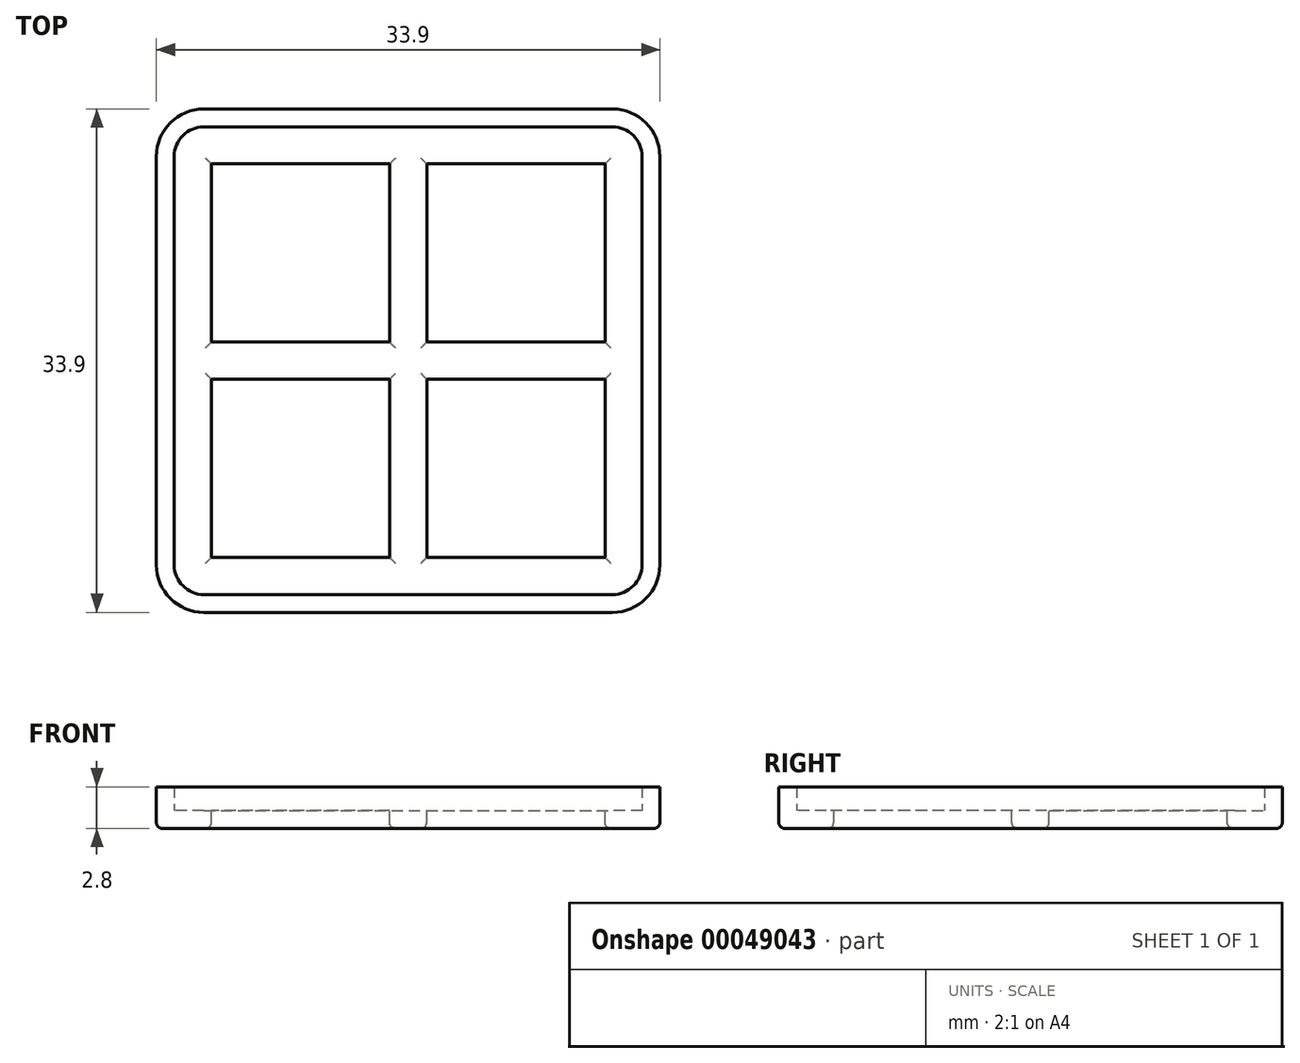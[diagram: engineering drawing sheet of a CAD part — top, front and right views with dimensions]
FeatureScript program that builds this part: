
annotation { "Feature Type Name" : "Feature", "Feature Type Description" : "" }
export const myFeature = defineFeature(function(context is Context, id is Id, definition is map)
    precondition{}
    {
        {
            var Q0;
            Q0=qCreatedBy(makeId("Top.planeOp"),FACE);
            var sketch = newSketch(context, id + "F0", { "sketchPlane" : qUnion([Q0])});
            skLineSegment(sketch, "E0.bottom", {"start": v(0, 0) * mm, "end": v(12, 0) * mm});
            skLineSegment(sketch, "E0.top", {"start": v(0, 12) * mm, "end": v(12, 12) * mm});
            skLineSegment(sketch, "E0.left", {"start": v(0, 0) * mm, "end": v(0, 12) * mm});
            skLineSegment(sketch, "E0.right", {"start": v(12, 0) * mm, "end": v(12, 12) * mm});
            skLineSegment(sketch, "E1.bottom", {"start": v(12, -2.5) * mm, "end": v(0, -2.5) * mm});
            skLineSegment(sketch, "E1.top", {"start": v(12, -14.5) * mm, "end": v(0, -14.5) * mm});
            skLineSegment(sketch, "E1.left", {"start": v(12, -2.5) * mm, "end": v(12, -14.5) * mm});
            skLineSegment(sketch, "E1.right", {"start": v(0, -2.5) * mm, "end": v(0, -14.5) * mm});
            skLineSegment(sketch, "E2.bottom", {"start": v(-2.5, 12) * mm, "end": v(-14.5, 12) * mm});
            skLineSegment(sketch, "E2.top", {"start": v(-2.5, 0) * mm, "end": v(-14.5, 0) * mm});
            skLineSegment(sketch, "E2.left", {"start": v(-2.5, 12) * mm, "end": v(-2.5, 0) * mm});
            skLineSegment(sketch, "E2.right", {"start": v(-14.5, 12) * mm, "end": v(-14.5, 0) * mm});
            skLineSegment(sketch, "E3.bottom", {"start": v(-2.5, -2.5) * mm, "end": v(-14.5, -2.5) * mm});
            skLineSegment(sketch, "E3.top", {"start": v(-2.5, -14.5) * mm, "end": v(-14.5, -14.5) * mm});
            skLineSegment(sketch, "E3.left", {"start": v(-2.5, -2.5) * mm, "end": v(-2.5, -14.5) * mm});
            skLineSegment(sketch, "E3.right", {"start": v(-14.5, -2.5) * mm, "end": v(-14.5, -14.5) * mm});
            skLineSegment(sketch, "E4.bottom", {"start": v(-15, 14.5) * mm, "end": v(12.5, 14.5) * mm});
            skLineSegment(sketch, "E4.top", {"start": v(-15, -17) * mm, "end": v(12.5, -17) * mm});
            skLineSegment(sketch, "E4.left", {"start": v(-17, 12.5) * mm, "end": v(-17, -15) * mm});
            skLineSegment(sketch, "E4.right", {"start": v(14.5, 12.5) * mm, "end": v(14.5, -15) * mm});
            skPoint(sketch, "E5.visualSharp", {"position": v(-17, 14.5) * mm});
            skArc(sketch, "E5.filletArc", {"start": v(-15, 14.5) * mm, "mid": v(-16.41, 13.91) * mm, "end": v(-17, 12.5) * mm});
            skPoint(sketch, "E6.visualSharp", {"position": v(14.5, 14.5) * mm});
            skArc(sketch, "E6.filletArc", {"start": v(14.5, 12.5) * mm, "mid": v(13.91, 13.91) * mm, "end": v(12.5, 14.5) * mm});
            skPoint(sketch, "E7.visualSharp", {"position": v(14.5, -17) * mm});
            skArc(sketch, "E7.filletArc", {"start": v(12.5, -17) * mm, "mid": v(13.91, -16.41) * mm, "end": v(14.5, -15) * mm});
            skPoint(sketch, "E8.visualSharp", {"position": v(-17, -17) * mm});
            skArc(sketch, "E8.filletArc", {"start": v(-17, -15) * mm, "mid": v(-16.41, -16.41) * mm, "end": v(-15, -17) * mm});
            skLineSegment(sketch, "E9.0", {"start": v(-15, 15.7) * mm, "end": v(12.5, 15.7) * mm});
            skArc(sketch, "E9.1", {"start": v(15.7, 12.5) * mm, "mid": v(14.76, 14.76) * mm, "end": v(12.5, 15.7) * mm});
            skArc(sketch, "E9.2", {"start": v(-15, 15.7) * mm, "mid": v(-17.26, 14.76) * mm, "end": v(-18.2, 12.5) * mm});
            skLineSegment(sketch, "E9.3", {"start": v(15.7, 12.5) * mm, "end": v(15.7, -15) * mm});
            skLineSegment(sketch, "E9.4", {"start": v(-18.2, 12.5) * mm, "end": v(-18.2, -15) * mm});
            skArc(sketch, "E9.5", {"start": v(-18.2, -15) * mm, "mid": v(-17.26, -17.26) * mm, "end": v(-15, -18.2) * mm});
            skLineSegment(sketch, "E9.6", {"start": v(-15, -18.2) * mm, "end": v(12.5, -18.2) * mm});
            skArc(sketch, "E9.7", {"start": v(12.5, -18.2) * mm, "mid": v(14.76, -17.26) * mm, "end": v(15.7, -15) * mm});
            skSolve(sketch);
        }
        {
            var Q0;
            Q0=makeQuery(id+"F0.imprint","IMPRINT",FACE,{"disambiguationData":[TD([[makeQuery(id+"F0.imprint","IMPRINT",EDGE,{"derivedFrom":sQuery(id+"F0.wireOp",EDGE,"E0.bottom")}),-1.0]])]});
            var Q1;
            Q1=makeQuery(id+"F0.imprint","IMPRINT",FACE,{"disambiguationData":[TD([[makeQuery(id+"F0.imprint","IMPRINT",EDGE,{"derivedFrom":sQuery(id+"F0.wireOp",EDGE,"E4.bottom")}),1.0]])]});
            extrude(context, id + "F1", {"entities" : qUnion([Q0, Q1]), "oppositeDirection" : true, "depth" : 1.2 * mm});
        }
        {
            var Q0;
            Q0=makeQuery(id+"F0.imprint","IMPRINT",FACE,{"disambiguationData":[TD([[makeQuery(id+"F0.imprint","IMPRINT",EDGE,{"derivedFrom":sQuery(id+"F0.wireOp",EDGE,"E4.bottom")}),1.0]])]});
            extrude(context, id + "F2", {"entities" : qUnion([Q0]), "operationType" : NewBodyOperationType.ADD, "depth" : 1.6 * mm});
        }
        {
            var Q0;
            Q0=makeQuery(id+"F1.opExtrude","CAP_FACE",FACE,{"disambiguationData":[OSD([sQuery(id+"F0.wireOp",EDGE,"E0.bottom"),sQuery(id+"F0.wireOp",EDGE,"E0.top"),sQuery(id+"F0.wireOp",EDGE,"E0.left"),sQuery(id+"F0.wireOp",EDGE,"E0.right"),sQuery(id+"F0.wireOp",EDGE,"E1.bottom"),sQuery(id+"F0.wireOp",EDGE,"E1.top"),sQuery(id+"F0.wireOp",EDGE,"E1.left"),sQuery(id+"F0.wireOp",EDGE,"E1.right"),sQuery(id+"F0.wireOp",EDGE,"E2.bottom"),sQuery(id+"F0.wireOp",EDGE,"E2.top"),sQuery(id+"F0.wireOp",EDGE,"E2.left"),sQuery(id+"F0.wireOp",EDGE,"E2.right"),sQuery(id+"F0.wireOp",EDGE,"E3.bottom"),sQuery(id+"F0.wireOp",EDGE,"E3.top"),sQuery(id+"F0.wireOp",EDGE,"E3.left"),sQuery(id+"F0.wireOp",EDGE,"E3.right"),sQuery(id+"F0.wireOp",EDGE,"E9.0"),sQuery(id+"F0.wireOp",EDGE,"E9.1"),sQuery(id+"F0.wireOp",EDGE,"E9.2"),sQuery(id+"F0.wireOp",EDGE,"E9.3"),sQuery(id+"F0.wireOp",EDGE,"E9.4"),sQuery(id+"F0.wireOp",EDGE,"E9.5"),sQuery(id+"F0.wireOp",EDGE,"E9.6"),sQuery(id+"F0.wireOp",EDGE,"E9.7")])],"isStart":false});
            fillet(context, id + "F3", {"entities" : qUnion([Q0]), "radius" : .4 * mm, "tangentPropagation" : true, "allowEdgeOverflow" : false});
        }
    });
